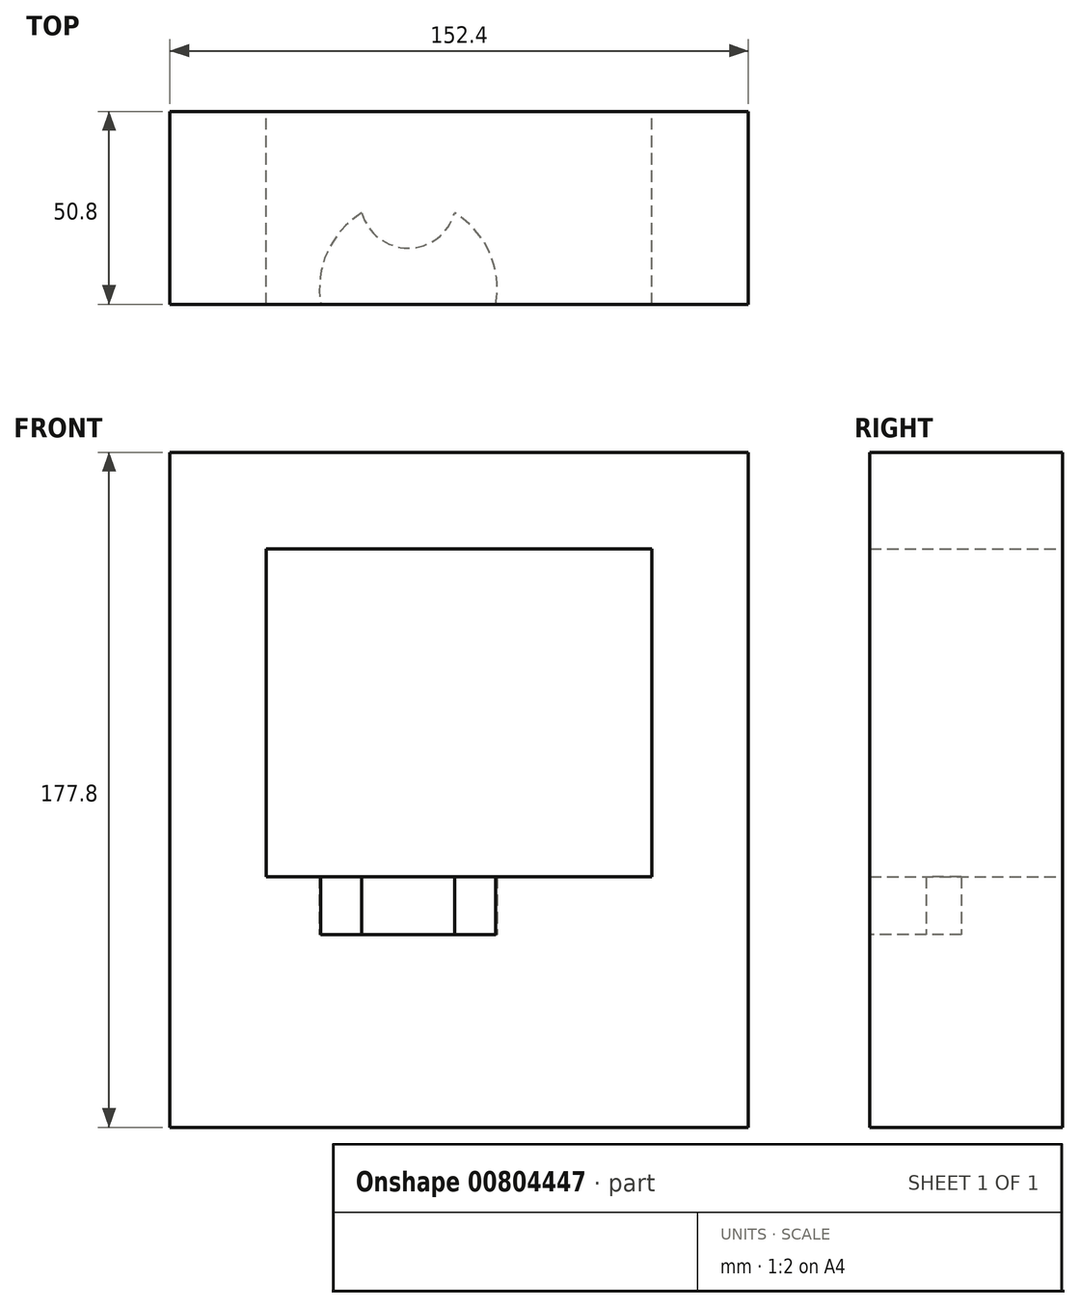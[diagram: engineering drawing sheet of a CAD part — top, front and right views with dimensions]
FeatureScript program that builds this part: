
annotation { "Feature Type Name" : "Feature", "Feature Type Description" : "" }
export const myFeature = defineFeature(function(context is Context, id is Id, definition is map)
    precondition{}
    {
        {
            var Q0;
            Q0=qCreatedBy(makeId("Front.planeOp"),FACE);
            var sketch = newSketch(context, id + "F0", { "sketchPlane" : qUnion([Q0])});
            skLineSegment(sketch, "E0.bottom", {"start": v(38.4, -109.6) * mm, "end": v(-114, -109.6) * mm});
            skLineSegment(sketch, "E0.top", {"start": v(38.4, 42.8) * mm, "end": v(-114, 42.8) * mm});
            skLineSegment(sketch, "E0.left", {"start": v(38.4, -109.6) * mm, "end": v(38.4, 42.8) * mm});
            skLineSegment(sketch, "E0.right", {"start": v(-114, -109.6) * mm, "end": v(-114, 42.8) * mm});
            skPoint(sketch, "E0.middle", {"position": v(-37.8, -33.4) * mm});
            skLineSegment(sketch, "E1.bottom", {"start": v(-88.6, 17.4) * mm, "end": v(13, 17.4) * mm});
            skLineSegment(sketch, "E1.top", {"start": v(-88.6, -84.2) * mm, "end": v(13, -84.2) * mm});
            skLineSegment(sketch, "E1.left", {"start": v(-88.6, 17.4) * mm, "end": v(-88.6, -84.2) * mm});
            skLineSegment(sketch, "E1.right", {"start": v(13, 17.4) * mm, "end": v(13, -84.2) * mm});
            skSolve(sketch);
        }
        {
            var Q0;
            Q0 = qSketchRegion(id + "F0", true);
            extrude(context, id + "F1", {"entities" : qUnion([Q0]), "depth" : 25.4 * mm, "offsetDistance" : 25.4 * mm});
        }
        {
            var Q0;
            Q0=makeQuery(id+"F1.opExtrude","CAP_FACE",FACE,{"disambiguationData":[OSD([sQuery(id+"F0.wireOp",EDGE,"E0.bottom"),sQuery(id+"F0.wireOp",EDGE,"E0.top"),sQuery(id+"F0.wireOp",EDGE,"E0.left"),sQuery(id+"F0.wireOp",EDGE,"E0.right"),sQuery(id+"F0.wireOp",EDGE,"E1.bottom"),sQuery(id+"F0.wireOp",EDGE,"E1.top"),sQuery(id+"F0.wireOp",EDGE,"E1.left"),sQuery(id+"F0.wireOp",EDGE,"E1.right")])],"isStart":false});
            var sketch = newSketch(context, id + "F2", { "sketchPlane" : qUnion([Q0])});
            skSolve(sketch);
        }
        {
            var Q0;
            Q0=makeQuery(id+"F2.imprint","IMPRINT",FACE,{"disambiguationData":[TD([[makeQuery(id+"F2.imprint","IMPRINT",EDGE,{"derivedFrom":makeQuery(id+"F1.opExtrude","CAP_EDGE",EDGE,{"disambiguationData":[OSD([sQuery(id+"F0.wireOp",EDGE,"E0.bottom")])],"isStart":false})}),-1.0]])]});
            var Q1;
            Q1=makeQuery(id+"F1.opExtrude","CAP_FACE",FACE,{"disambiguationData":[OSD([sQuery(id+"F0.wireOp",EDGE,"E0.bottom"),sQuery(id+"F0.wireOp",EDGE,"E0.top"),sQuery(id+"F0.wireOp",EDGE,"E0.left"),sQuery(id+"F0.wireOp",EDGE,"E0.right"),sQuery(id+"F0.wireOp",EDGE,"E1.bottom"),sQuery(id+"F0.wireOp",EDGE,"E1.top"),sQuery(id+"F0.wireOp",EDGE,"E1.left"),sQuery(id+"F0.wireOp",EDGE,"E1.right")])],"isStart":true});
            extrude(context, id + "F3", {"entities" : qUnion([Q0, Q1]), "operationType" : NewBodyOperationType.ADD, "depth" : 25.4 * mm, "offsetDistance" : 25.4 * mm});
        }
        {
            var Q0;
            {var subQ0=sQuery(id+"F0.wireOp",EDGE,"E0.bottom");Q0=makeQuery(id+"F3.boolean.opBoolean","MERGE",FACE,{"derivedFrom":[makeQuery(id+"F1.opExtrude","SWEPT_FACE",FACE,{"disambiguationData":[OSD([subQ0])]}),makeQuery(id+"F3.opExtrude","SWEPT_FACE",FACE,{"disambiguationData":[OSD([subQ0]),TDD([makeQuery(id+"F1.opExtrude","CAP_EDGE",EDGE,{"disambiguationData":[OSD([subQ0])],"isStart":true})])]}),makeQuery(id+"F3.opExtrude","SWEPT_FACE",FACE,{"disambiguationData":[OSD([subQ0]),TDD([makeQuery(id+"F2.imprint","IMPRINT",EDGE,{"derivedFrom":makeQuery(id+"F1.opExtrude","CAP_EDGE",EDGE,{"disambiguationData":[OSD([subQ0])],"isStart":false})})])]})]});}
            extrude(context, id + "F4", {"entities" : qUnion([Q0]), "operationType" : NewBodyOperationType.ADD, "depth" : 25.4 * mm, "offsetDistance" : 25.4 * mm});
        }
        {
            var Q0;
            Q0=makeQuery(id+"F4.opExtrude","CAP_FACE",FACE,{"disambiguationData":[OSD([sQuery(id+"F0.wireOp",EDGE,"E0.bottom")])],"isStart":false});
            var sketch = newSketch(context, id + "F5", { "sketchPlane" : qUnion([Q0])});
            skCircle(sketch, "E2", {"center": v(-51.2, 21.3) * mm, "radius": 23.41 * mm});
            skCircle(sketch, "E3", {"center": v(-51.2, -2.1) * mm, "radius": 12.7 * mm});
            skSolve(sketch);
        }
        {
            var Q0;
            {var subQ0=sQuery(id+"F5.wireOp",EDGE,"E3");var subQ1=sQuery(id+"F5.wireOp",EDGE,"E2");var subQ2=makeQuery(id+"F5.imprint","INTERSECT",VERTEX,{"disambiguationData":[OD(1.0)],"derivedFrom":[subQ1,subQ0]});Q0=makeQuery(id+"F5.imprint","IMPRINT",FACE,{"disambiguationData":[TD([[makeQuery(id+"F5.imprint","IMPRINT",EDGE,{"disambiguationData":[TD([[subQ2,1.0]])],"derivedFrom":subQ1}),-1.0]])]});}
            var Q1;
            {var subQ0=sQuery(id+"F5.wireOp",EDGE,"E3");var subQ1=sQuery(id+"F5.wireOp",EDGE,"E2");var subQ2=makeQuery(id+"F5.imprint","INTERSECT",VERTEX,{"disambiguationData":[OD(0.0)],"derivedFrom":[subQ1,subQ0]});Q1=makeQuery(id+"F5.imprint","IMPRINT",FACE,{"disambiguationData":[TD([[makeQuery(id+"F5.imprint","IMPRINT",EDGE,{"disambiguationData":[TD([[subQ2,1.0]])],"derivedFrom":subQ0}),1.0]])]});}
            var Q2;
            {var subQ0=sQuery(id+"F5.wireOp",EDGE,"E3");var subQ1=sQuery(id+"F5.wireOp",EDGE,"E2");var subQ2=makeQuery(id+"F5.imprint","INTERSECT",VERTEX,{"disambiguationData":[OD(0.0)],"derivedFrom":[subQ1,subQ0]});Q2=makeQuery(id+"F5.imprint","IMPRINT",FACE,{"disambiguationData":[TD([[makeQuery(id+"F5.imprint","IMPRINT",EDGE,{"disambiguationData":[TD([[subQ2,-1.0]])],"derivedFrom":subQ1}),-1.0]])]});}
            var Q3;
            {var subQ0=sQuery(id+"F5.wireOp",EDGE,"E2");var subQ1=sQuery(id+"F0.wireOp",EDGE,"E0.bottom");var subQ2=makeQuery(id+"F4.opExtrude","CAP_EDGE",EDGE,{"disambiguationData":[OSD([subQ1]),TDD([makeQuery(id+"F1.opExtrude","CAP_EDGE",EDGE,{"disambiguationData":[OSD([subQ1])],"isStart":true})])],"isStart":false});var subQ3=makeQuery(id+"F5.imprint","INTERSECT",VERTEX,{"disambiguationData":[OD(0.0)],"derivedFrom":[subQ2,subQ0]});Q3=makeQuery(id+"F5.imprint","IMPRINT",FACE,{"disambiguationData":[TD([[makeQuery(id+"F5.imprint","IMPRINT",EDGE,{"disambiguationData":[TD([[subQ3,-1.0]])],"derivedFrom":subQ0}),-1.0]])]});}
            var Q4;
            {var subQ0=sQuery(id+"F5.wireOp",EDGE,"E2");var subQ1=sQuery(id+"F0.wireOp",EDGE,"E0.bottom");var subQ2=makeQuery(id+"F4.opExtrude","CAP_EDGE",EDGE,{"disambiguationData":[OSD([subQ1]),TDD([makeQuery(id+"F1.opExtrude","CAP_EDGE",EDGE,{"disambiguationData":[OSD([subQ1])],"isStart":true})])],"isStart":false});var subQ3=makeQuery(id+"F5.imprint","INTERSECT",VERTEX,{"disambiguationData":[OD(0.0)],"derivedFrom":[subQ2,subQ0]});Q4=makeQuery(id+"F5.imprint","IMPRINT",FACE,{"disambiguationData":[TD([[makeQuery(id+"F5.imprint","IMPRINT",EDGE,{"disambiguationData":[TD([[subQ3,-1.0]])],"derivedFrom":subQ0}),1.0]])]});}
            var Q5;
            {var subQ0=sQuery(id+"F5.wireOp",EDGE,"E3");var subQ1=sQuery(id+"F5.wireOp",EDGE,"E2");var subQ2=makeQuery(id+"F5.imprint","INTERSECT",VERTEX,{"disambiguationData":[OD(0.0)],"derivedFrom":[subQ1,subQ0]});Q5=makeQuery(id+"F5.imprint","IMPRINT",FACE,{"disambiguationData":[TD([[makeQuery(id+"F5.imprint","IMPRINT",EDGE,{"disambiguationData":[TD([[subQ2,1.0]])],"derivedFrom":subQ1}),1.0]])]});}
            extrude(context, id + "F6", {"entities" : qUnion([Q0, Q1, Q2, Q3, Q4, Q5]), "operationType" : NewBodyOperationType.ADD, "oppositeDirection" : true, "depth" : 65.93 * mm, "offsetDistance" : 25.4 * mm});
        }
    });
